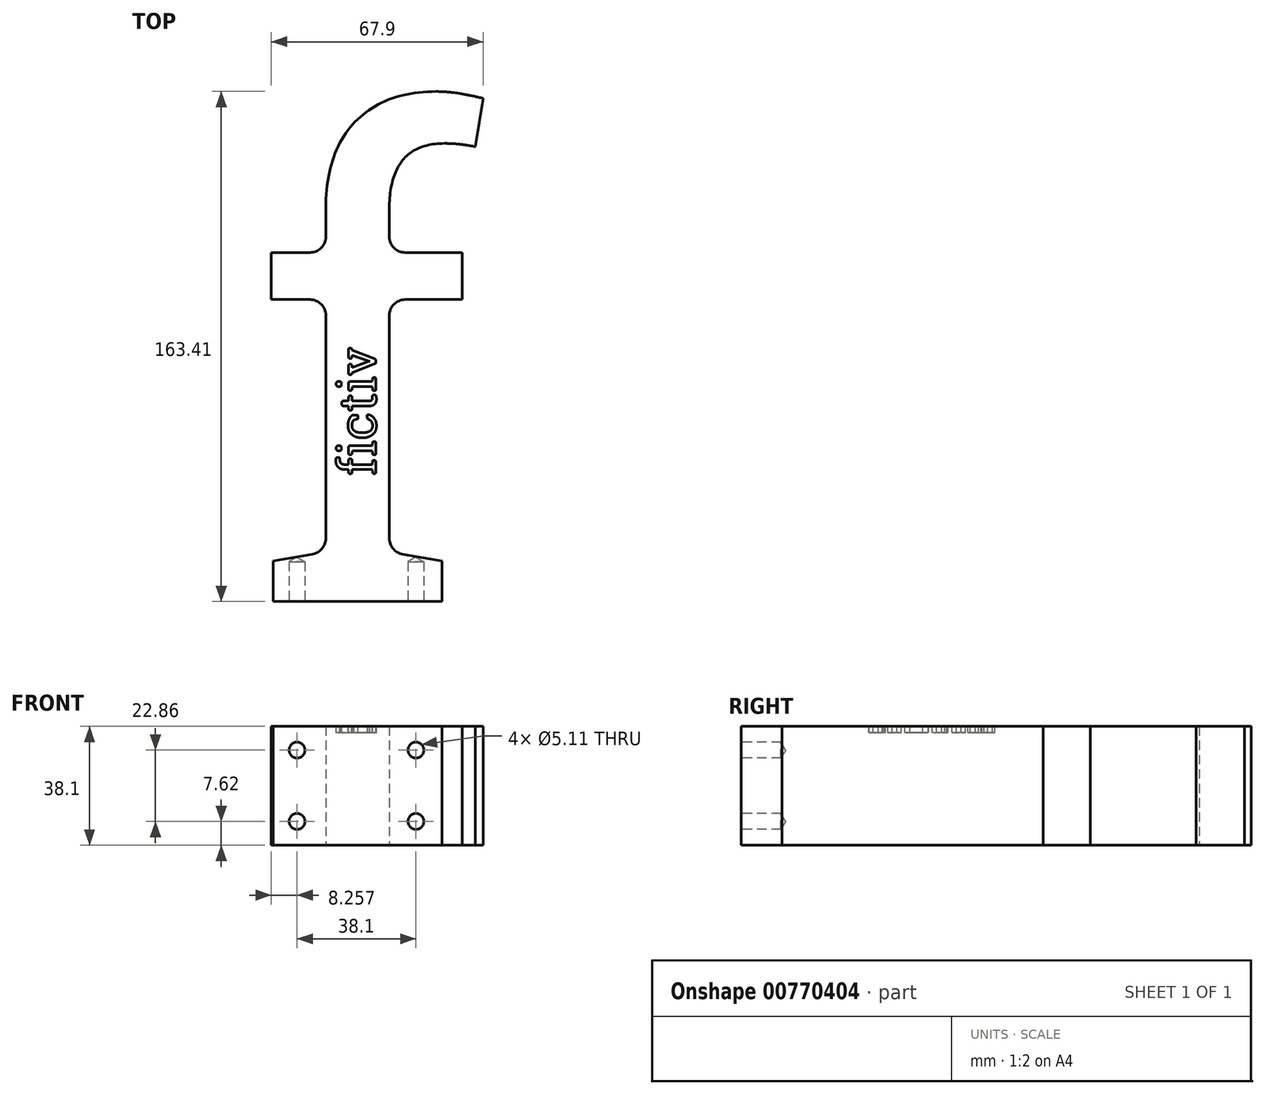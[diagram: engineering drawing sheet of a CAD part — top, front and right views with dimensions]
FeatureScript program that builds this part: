
annotation { "Feature Type Name" : "Feature", "Feature Type Description" : "" }
export const myFeature = defineFeature(function(context is Context, id is Id, definition is map)
    precondition{}
    {
        {
            var Q0;
            Q0=qCreatedBy(makeId("Top.planeOp"),FACE);
            var sketch = newSketch(context, id + "F0", { "sketchPlane" : qUnion([Q0])});
            skText(sketch, "E0", { "text": "f", "fontName": "RobotoSlab-Regular.ttf"});
            const initialGuessF0  = {"E0": [-0.0585, -0.07017, 1, 0, 0.1524]};
            skSetInitialGuess(sketch, initialGuessF0);
            skSolve(sketch);
        }
        {
            var Q0;
            Q0 = qSketchRegion(id + "F0", true);
            extrude(context, id + "F1", {"entities" : qUnion([Q0]), "depth" : 38.1 * mm, "offsetDistance" : 25 * mm});
        }
        {
            var Q0;
            Q0=makeQuery(id+"F1.opExtrude","SWEPT_EDGE",EDGE,{"disambiguationData":[OSD([sQuery(id+"F0.wireOp",EDGE,"E0.sketch_text.stroke-15"),sQuery(id+"F0.wireOp",EDGE,"E0.sketch_text.stroke-16")])]});
            var Q1;
            Q1=makeQuery(id+"F1.opExtrude","SWEPT_EDGE",EDGE,{"disambiguationData":[OSD([sQuery(id+"F0.wireOp",EDGE,"E0.sketch_text.stroke-22"),sQuery(id+"F0.wireOp",EDGE,"E0.sketch_text.stroke-23")])]});
            var Q2;
            Q2=makeQuery(id+"F1.opExtrude","SWEPT_EDGE",EDGE,{"disambiguationData":[OSD([sQuery(id+"F0.wireOp",EDGE,"E0.sketch_text.stroke-1"),sQuery(id+"F0.wireOp",EDGE,"E0.sketch_text.stroke-2")])]});
            var Q3;
            Q3=makeQuery(id+"F1.opExtrude","SWEPT_EDGE",EDGE,{"disambiguationData":[OSD([sQuery(id+"F0.wireOp",EDGE,"E0.sketch_text.stroke-12"),sQuery(id+"F0.wireOp",EDGE,"E0.sketch_text.stroke-13")])]});
            var Q4;
            Q4=makeQuery(id+"F1.opExtrude","SWEPT_EDGE",EDGE,{"disambiguationData":[OSD([sQuery(id+"F0.wireOp",EDGE,"E0.sketch_text.stroke-16"),sQuery(id+"F0.wireOp",EDGE,"E0.sketch_text.stroke-17")])]});
            var Q5;
            Q5=makeQuery(id+"F1.opExtrude","SWEPT_EDGE",EDGE,{"disambiguationData":[OSD([sQuery(id+"F0.wireOp",EDGE,"E0.sketch_text.stroke-21"),sQuery(id+"F0.wireOp",EDGE,"E0.sketch_text.stroke-22")])]});
            fillet(context, id + "F2", {"entities" : qUnion([Q0, Q1, Q2, Q3, Q4, Q5]), "radius" : 5.08 * mm, "tangentPropagation" : true, "allowEdgeOverflow" : false});
        }
        {
            var Q0;
            Q0=makeQuery(id+"F1.opExtrude","SWEPT_FACE",FACE,{"disambiguationData":[OSD([sQuery(id+"F0.wireOp",EDGE,"E0.sketch_text.stroke-19")])]});
            var sketch = newSketch(context, id + "F3", { "sketchPlane" : qUnion([Q0])});
            skPoint(sketch, "E1", {"position": v(-43, 7.62) * mm});
            skPoint(sketch, "E2", {"position": v(-43, 30.48) * mm});
            skPoint(sketch, "E3", {"position": v(-4.9, 30.48) * mm});
            skPoint(sketch, "E4", {"position": v(-4.9, 7.62) * mm});
            skSolve(sketch);
        }
        {
            var Q0;
            Q0=sQuery(id+"F3.wireOp",VERTEX,"E2");
            var Q1;
            Q1=sQuery(id+"F3.wireOp",VERTEX,"E1");
            var Q2;
            Q2=sQuery(id+"F3.wireOp",VERTEX,"E4");
            var Q3;
            Q3=sQuery(id+"F3.wireOp",VERTEX,"E3");
            var Q4;
            Q4=makeQuery(id+"F1.opExtrude","SWEPT_BODY",BODY,{"disambiguationData":[OSD([sQuery(id+"F0.wireOp",EDGE,"E0.sketch_text.stroke-0"),sQuery(id+"F0.wireOp",EDGE,"E0.sketch_text.stroke-1"),sQuery(id+"F0.wireOp",EDGE,"E0.sketch_text.stroke-2"),sQuery(id+"F0.wireOp",EDGE,"E0.sketch_text.stroke-3"),sQuery(id+"F0.wireOp",EDGE,"E0.sketch_text.stroke-4"),sQuery(id+"F0.wireOp",EDGE,"E0.sketch_text.stroke-5"),sQuery(id+"F0.wireOp",EDGE,"E0.sketch_text.stroke-6"),sQuery(id+"F0.wireOp",EDGE,"E0.sketch_text.stroke-7"),sQuery(id+"F0.wireOp",EDGE,"E0.sketch_text.stroke-8"),sQuery(id+"F0.wireOp",EDGE,"E0.sketch_text.stroke-9"),sQuery(id+"F0.wireOp",EDGE,"E0.sketch_text.stroke-10"),sQuery(id+"F0.wireOp",EDGE,"E0.sketch_text.stroke-11"),sQuery(id+"F0.wireOp",EDGE,"E0.sketch_text.stroke-12"),sQuery(id+"F0.wireOp",EDGE,"E0.sketch_text.stroke-13"),sQuery(id+"F0.wireOp",EDGE,"E0.sketch_text.stroke-14"),sQuery(id+"F0.wireOp",EDGE,"E0.sketch_text.stroke-15"),sQuery(id+"F0.wireOp",EDGE,"E0.sketch_text.stroke-16"),sQuery(id+"F0.wireOp",EDGE,"E0.sketch_text.stroke-17"),sQuery(id+"F0.wireOp",EDGE,"E0.sketch_text.stroke-18"),sQuery(id+"F0.wireOp",EDGE,"E0.sketch_text.stroke-19"),sQuery(id+"F0.wireOp",EDGE,"E0.sketch_text.stroke-20"),sQuery(id+"F0.wireOp",EDGE,"E0.sketch_text.stroke-21"),sQuery(id+"F0.wireOp",EDGE,"E0.sketch_text.stroke-22"),sQuery(id+"F0.wireOp",EDGE,"E0.sketch_text.stroke-23")])]});
            hole(context, id + "F4", {"style" : HoleStyle.SIMPLE, "endStyle" : HoleEndStyle.BLIND, "standardTappedOrClearance" : lookupTablePath({ "standard" : "ANSI", "engagement" : "75%", "pitch" : "20 tpi", "size" : "1/4", "type" : "Tapped" }), "standardBlindInLast" : lookupTablePath({ "standard" : "ANSI", "engagement" : "75%", "pitch" : "20 tpi", "size" : "1/4", "type" : "Tapped" }), "holeDiameter" : 5.1 * mm, "majorDiameter" : 6.35 * mm, "showTappedDepth" : true, "holeDepth" : 12.7 * mm, "isTappedThrough" : true, "tappedDepth" : 8.9 * mm, "tapClearance" : 3, "locations" : qUnion([Q0, Q1, Q2, Q3]), "scope" : qUnion([Q4])});
        }
        {
            var Q0;
            Q0=makeQuery(id+"F1.opExtrude","CAP_FACE",FACE,{"disambiguationData":[OSD([sQuery(id+"F0.wireOp",EDGE,"E0.sketch_text.stroke-0"),sQuery(id+"F0.wireOp",EDGE,"E0.sketch_text.stroke-1"),sQuery(id+"F0.wireOp",EDGE,"E0.sketch_text.stroke-2"),sQuery(id+"F0.wireOp",EDGE,"E0.sketch_text.stroke-3"),sQuery(id+"F0.wireOp",EDGE,"E0.sketch_text.stroke-4"),sQuery(id+"F0.wireOp",EDGE,"E0.sketch_text.stroke-5"),sQuery(id+"F0.wireOp",EDGE,"E0.sketch_text.stroke-6"),sQuery(id+"F0.wireOp",EDGE,"E0.sketch_text.stroke-7"),sQuery(id+"F0.wireOp",EDGE,"E0.sketch_text.stroke-8"),sQuery(id+"F0.wireOp",EDGE,"E0.sketch_text.stroke-9"),sQuery(id+"F0.wireOp",EDGE,"E0.sketch_text.stroke-10"),sQuery(id+"F0.wireOp",EDGE,"E0.sketch_text.stroke-11"),sQuery(id+"F0.wireOp",EDGE,"E0.sketch_text.stroke-12"),sQuery(id+"F0.wireOp",EDGE,"E0.sketch_text.stroke-13"),sQuery(id+"F0.wireOp",EDGE,"E0.sketch_text.stroke-14"),sQuery(id+"F0.wireOp",EDGE,"E0.sketch_text.stroke-15"),sQuery(id+"F0.wireOp",EDGE,"E0.sketch_text.stroke-16"),sQuery(id+"F0.wireOp",EDGE,"E0.sketch_text.stroke-17"),sQuery(id+"F0.wireOp",EDGE,"E0.sketch_text.stroke-18"),sQuery(id+"F0.wireOp",EDGE,"E0.sketch_text.stroke-19"),sQuery(id+"F0.wireOp",EDGE,"E0.sketch_text.stroke-20"),sQuery(id+"F0.wireOp",EDGE,"E0.sketch_text.stroke-21"),sQuery(id+"F0.wireOp",EDGE,"E0.sketch_text.stroke-22"),sQuery(id+"F0.wireOp",EDGE,"E0.sketch_text.stroke-23")])],"isStart":false});
            var sketch = newSketch(context, id + "F5", { "sketchPlane" : qUnion([Q0])});
            skText(sketch, "E5", { "text": "fictiv", "fontName": "RobotoSlab-Regular.ttf"});
            const initialGuessF5  = {"E5": [-0.01771, -0.02984, 0, 1, 0.012]};
            skSetInitialGuess(sketch, initialGuessF5);
            skSolve(sketch);
        }
        {
            var Q0;
            Q0 = qSketchRegion(id + "F5", true);
            var Q1;
            Q1 = qConstructionFilter(qBodyType(qCreatedBy(id + "F5" ,EDGE), BodyType.WIRE), ConstructionObject.NO);
            extrude(context, id + "F6", {"entities" : qUnion([Q0]), "operationType" : NewBodyOperationType.REMOVE, "surfaceEntities" : qUnion([Q1]), "depth" : -2 * mm, "offsetDistance" : 25 * mm});
        }
        {
            var Q0;
            Q0=makeQuery(id+"F6.boolean.opBoolean","COPY",EDGE,{"derivedFrom":makeQuery(id+"F6.opExtrude","SWEPT_EDGE",EDGE,{"disambiguationData":[OSD([sQuery(id+"F5.wireOp",EDGE,"E5.sketch_text.stroke-0"),sQuery(id+"F5.wireOp",EDGE,"E5.sketch_text.stroke-1")])]})});
            var Q1;
            Q1=makeQuery(id+"F6.boolean.opBoolean","COPY",EDGE,{"derivedFrom":makeQuery(id+"F6.opExtrude","SWEPT_EDGE",EDGE,{"disambiguationData":[OSD([sQuery(id+"F5.wireOp",EDGE,"E5.sketch_text.stroke-20"),sQuery(id+"F5.wireOp",EDGE,"E5.sketch_text.stroke-21")])]})});
            var Q2;
            Q2=makeQuery(id+"F6.boolean.opBoolean","COPY",EDGE,{"derivedFrom":makeQuery(id+"F6.opExtrude","SWEPT_EDGE",EDGE,{"disambiguationData":[OSD([sQuery(id+"F5.wireOp",EDGE,"E5.sketch_text.stroke-24"),sQuery(id+"F5.wireOp",EDGE,"E5.sketch_text.stroke-33")])]})});
            var Q3;
            Q3=makeQuery(id+"F6.boolean.opBoolean","COPY",EDGE,{"derivedFrom":makeQuery(id+"F6.opExtrude","SWEPT_EDGE",EDGE,{"disambiguationData":[OSD([sQuery(id+"F5.wireOp",EDGE,"E5.sketch_text.stroke-27"),sQuery(id+"F5.wireOp",EDGE,"E5.sketch_text.stroke-28")])]})});
            var Q4;
            Q4=makeQuery(id+"F6.boolean.opBoolean","COPY",EDGE,{"derivedFrom":makeQuery(id+"F6.opExtrude","SWEPT_EDGE",EDGE,{"disambiguationData":[OSD([sQuery(id+"F5.wireOp",EDGE,"E5.sketch_text.stroke-77"),sQuery(id+"F5.wireOp",EDGE,"E5.sketch_text.stroke-78")])]})});
            var Q5;
            Q5=makeQuery(id+"F6.boolean.opBoolean","COPY",EDGE,{"derivedFrom":makeQuery(id+"F6.opExtrude","SWEPT_EDGE",EDGE,{"disambiguationData":[OSD([sQuery(id+"F5.wireOp",EDGE,"E5.sketch_text.stroke-79"),sQuery(id+"F5.wireOp",EDGE,"E5.sketch_text.stroke-80")])]})});
            var Q6;
            Q6=makeQuery(id+"F6.boolean.opBoolean","COPY",EDGE,{"derivedFrom":makeQuery(id+"F6.opExtrude","SWEPT_EDGE",EDGE,{"disambiguationData":[OSD([sQuery(id+"F5.wireOp",EDGE,"E5.sketch_text.stroke-84"),sQuery(id+"F5.wireOp",EDGE,"E5.sketch_text.stroke-85")])]})});
            var Q7;
            Q7=makeQuery(id+"F6.boolean.opBoolean","COPY",EDGE,{"derivedFrom":makeQuery(id+"F6.opExtrude","SWEPT_EDGE",EDGE,{"disambiguationData":[OSD([sQuery(id+"F5.wireOp",EDGE,"E5.sketch_text.stroke-35"),sQuery(id+"F5.wireOp",EDGE,"E5.sketch_text.stroke-36")])]})});
            var Q8;
            Q8=makeQuery(id+"F6.boolean.opBoolean","COPY",EDGE,{"derivedFrom":makeQuery(id+"F6.opExtrude","SWEPT_EDGE",EDGE,{"disambiguationData":[OSD([sQuery(id+"F5.wireOp",EDGE,"E5.sketch_text.stroke-81"),sQuery(id+"F5.wireOp",EDGE,"E5.sketch_text.stroke-90")])]})});
            var Q9;
            Q9=makeQuery(id+"F6.boolean.opBoolean","COPY",EDGE,{"derivedFrom":makeQuery(id+"F6.opExtrude","SWEPT_EDGE",EDGE,{"disambiguationData":[OSD([sQuery(id+"F5.wireOp",EDGE,"E5.sketch_text.stroke-92"),sQuery(id+"F5.wireOp",EDGE,"E5.sketch_text.stroke-93")])]})});
            var Q10;
            Q10=makeQuery(id+"F6.boolean.opBoolean","COPY",EDGE,{"derivedFrom":makeQuery(id+"F6.opExtrude","SWEPT_EDGE",EDGE,{"disambiguationData":[OSD([sQuery(id+"F5.wireOp",EDGE,"E5.sketch_text.stroke-110"),sQuery(id+"F5.wireOp",EDGE,"E5.sketch_text.stroke-111")])]})});
            var Q11;
            Q11=makeQuery(id+"F6.boolean.opBoolean","COPY",EDGE,{"derivedFrom":makeQuery(id+"F6.opExtrude","SWEPT_EDGE",EDGE,{"disambiguationData":[OSD([sQuery(id+"F5.wireOp",EDGE,"E5.sketch_text.stroke-102"),sQuery(id+"F5.wireOp",EDGE,"E5.sketch_text.stroke-103")])]})});
            var Q12;
            Q12=makeQuery(id+"F6.boolean.opBoolean","COPY",EDGE,{"derivedFrom":makeQuery(id+"F6.opExtrude","SWEPT_EDGE",EDGE,{"disambiguationData":[OSD([sQuery(id+"F5.wireOp",EDGE,"E5.sketch_text.stroke-19"),sQuery(id+"F5.wireOp",EDGE,"E5.sketch_text.stroke-20")])]})});
            var Q13;
            Q13=makeQuery(id+"F6.boolean.opBoolean","COPY",EDGE,{"derivedFrom":makeQuery(id+"F6.opExtrude","SWEPT_EDGE",EDGE,{"disambiguationData":[OSD([sQuery(id+"F5.wireOp",EDGE,"E5.sketch_text.stroke-0"),sQuery(id+"F5.wireOp",EDGE,"E5.sketch_text.stroke-23")])]})});
            var Q14;
            Q14=makeQuery(id+"F6.boolean.opBoolean","COPY",EDGE,{"derivedFrom":makeQuery(id+"F6.opExtrude","SWEPT_EDGE",EDGE,{"disambiguationData":[OSD([sQuery(id+"F5.wireOp",EDGE,"E5.sketch_text.stroke-32"),sQuery(id+"F5.wireOp",EDGE,"E5.sketch_text.stroke-33")])]})});
            var Q15;
            Q15=makeQuery(id+"F6.boolean.opBoolean","COPY",EDGE,{"derivedFrom":makeQuery(id+"F6.opExtrude","SWEPT_EDGE",EDGE,{"disambiguationData":[OSD([sQuery(id+"F5.wireOp",EDGE,"E5.sketch_text.stroke-26"),sQuery(id+"F5.wireOp",EDGE,"E5.sketch_text.stroke-27")])]})});
            var Q16;
            Q16=makeQuery(id+"F6.boolean.opBoolean","COPY",EDGE,{"derivedFrom":makeQuery(id+"F6.opExtrude","SWEPT_EDGE",EDGE,{"disambiguationData":[OSD([sQuery(id+"F5.wireOp",EDGE,"E5.sketch_text.stroke-34"),sQuery(id+"F5.wireOp",EDGE,"E5.sketch_text.stroke-35")])]})});
            var Q17;
            Q17=makeQuery(id+"F6.boolean.opBoolean","COPY",EDGE,{"derivedFrom":makeQuery(id+"F6.opExtrude","SWEPT_EDGE",EDGE,{"disambiguationData":[OSD([sQuery(id+"F5.wireOp",EDGE,"E5.sketch_text.stroke-76"),sQuery(id+"F5.wireOp",EDGE,"E5.sketch_text.stroke-77")])]})});
            var Q18;
            Q18=makeQuery(id+"F6.boolean.opBoolean","COPY",EDGE,{"derivedFrom":makeQuery(id+"F6.opExtrude","SWEPT_EDGE",EDGE,{"disambiguationData":[OSD([sQuery(id+"F5.wireOp",EDGE,"E5.sketch_text.stroke-91"),sQuery(id+"F5.wireOp",EDGE,"E5.sketch_text.stroke-92")])]})});
            var Q19;
            Q19=makeQuery(id+"F6.boolean.opBoolean","COPY",EDGE,{"derivedFrom":makeQuery(id+"F6.opExtrude","SWEPT_EDGE",EDGE,{"disambiguationData":[OSD([sQuery(id+"F5.wireOp",EDGE,"E5.sketch_text.stroke-83"),sQuery(id+"F5.wireOp",EDGE,"E5.sketch_text.stroke-84")])]})});
            var Q20;
            Q20=makeQuery(id+"F6.boolean.opBoolean","COPY",EDGE,{"derivedFrom":makeQuery(id+"F6.opExtrude","SWEPT_EDGE",EDGE,{"disambiguationData":[OSD([sQuery(id+"F5.wireOp",EDGE,"E5.sketch_text.stroke-89"),sQuery(id+"F5.wireOp",EDGE,"E5.sketch_text.stroke-90")])]})});
            var Q21;
            Q21=makeQuery(id+"F6.boolean.opBoolean","COPY",EDGE,{"derivedFrom":makeQuery(id+"F6.opExtrude","SWEPT_EDGE",EDGE,{"disambiguationData":[OSD([sQuery(id+"F5.wireOp",EDGE,"E5.sketch_text.stroke-109"),sQuery(id+"F5.wireOp",EDGE,"E5.sketch_text.stroke-110")])]})});
            var Q22;
            Q22=makeQuery(id+"F6.boolean.opBoolean","COPY",EDGE,{"derivedFrom":makeQuery(id+"F6.opExtrude","SWEPT_EDGE",EDGE,{"disambiguationData":[OSD([sQuery(id+"F5.wireOp",EDGE,"E5.sketch_text.stroke-107"),sQuery(id+"F5.wireOp",EDGE,"E5.sketch_text.stroke-108")])]})});
            var Q23;
            Q23=makeQuery(id+"F6.boolean.opBoolean","COPY",EDGE,{"derivedFrom":makeQuery(id+"F6.opExtrude","SWEPT_EDGE",EDGE,{"disambiguationData":[OSD([sQuery(id+"F5.wireOp",EDGE,"E5.sketch_text.stroke-52"),sQuery(id+"F5.wireOp",EDGE,"E5.sketch_text.stroke-53")])]})});
            var Q24;
            Q24=makeQuery(id+"F6.boolean.opBoolean","COPY",EDGE,{"derivedFrom":makeQuery(id+"F6.opExtrude","SWEPT_EDGE",EDGE,{"disambiguationData":[OSD([sQuery(id+"F5.wireOp",EDGE,"E5.sketch_text.stroke-18"),sQuery(id+"F5.wireOp",EDGE,"E5.sketch_text.stroke-19")])]})});
            var Q25;
            Q25=makeQuery(id+"F6.boolean.opBoolean","COPY",EDGE,{"derivedFrom":makeQuery(id+"F6.opExtrude","SWEPT_EDGE",EDGE,{"disambiguationData":[OSD([sQuery(id+"F5.wireOp",EDGE,"E5.sketch_text.stroke-31"),sQuery(id+"F5.wireOp",EDGE,"E5.sketch_text.stroke-32")])]})});
            var Q26;
            Q26=makeQuery(id+"F6.boolean.opBoolean","COPY",EDGE,{"derivedFrom":makeQuery(id+"F6.opExtrude","SWEPT_EDGE",EDGE,{"disambiguationData":[OSD([sQuery(id+"F5.wireOp",EDGE,"E5.sketch_text.stroke-51"),sQuery(id+"F5.wireOp",EDGE,"E5.sketch_text.stroke-52")])]})});
            var Q27;
            Q27=makeQuery(id+"F6.boolean.opBoolean","COPY",EDGE,{"derivedFrom":makeQuery(id+"F6.opExtrude","SWEPT_EDGE",EDGE,{"disambiguationData":[OSD([sQuery(id+"F5.wireOp",EDGE,"E5.sketch_text.stroke-70"),sQuery(id+"F5.wireOp",EDGE,"E5.sketch_text.stroke-71")])]})});
            var Q28;
            Q28=makeQuery(id+"F6.boolean.opBoolean","COPY",EDGE,{"derivedFrom":makeQuery(id+"F6.opExtrude","SWEPT_EDGE",EDGE,{"disambiguationData":[OSD([sQuery(id+"F5.wireOp",EDGE,"E5.sketch_text.stroke-88"),sQuery(id+"F5.wireOp",EDGE,"E5.sketch_text.stroke-89")])]})});
            var Q29;
            Q29=makeQuery(id+"F6.boolean.opBoolean","COPY",EDGE,{"derivedFrom":makeQuery(id+"F6.opExtrude","SWEPT_EDGE",EDGE,{"disambiguationData":[OSD([sQuery(id+"F5.wireOp",EDGE,"E5.sketch_text.stroke-106"),sQuery(id+"F5.wireOp",EDGE,"E5.sketch_text.stroke-107")])]})});
            var Q30;
            Q30=makeQuery(id+"F6.boolean.opBoolean","COPY",EDGE,{"derivedFrom":makeQuery(id+"F6.opExtrude","SWEPT_EDGE",EDGE,{"disambiguationData":[OSD([sQuery(id+"F5.wireOp",EDGE,"E5.sketch_text.stroke-104"),sQuery(id+"F5.wireOp",EDGE,"E5.sketch_text.stroke-105")])]})});
            var Q31;
            Q31=makeQuery(id+"F6.boolean.opBoolean","COPY",EDGE,{"derivedFrom":makeQuery(id+"F6.opExtrude","SWEPT_EDGE",EDGE,{"disambiguationData":[OSD([sQuery(id+"F5.wireOp",EDGE,"E5.sketch_text.stroke-95"),sQuery(id+"F5.wireOp",EDGE,"E5.sketch_text.stroke-112")])]})});
            var Q32;
            Q32=makeQuery(id+"F6.boolean.opBoolean","COPY",EDGE,{"derivedFrom":makeQuery(id+"F6.opExtrude","SWEPT_EDGE",EDGE,{"disambiguationData":[OSD([sQuery(id+"F5.wireOp",EDGE,"E5.sketch_text.stroke-91"),sQuery(id+"F5.wireOp",EDGE,"E5.sketch_text.stroke-94")])]})});
            var Q33;
            Q33=makeQuery(id+"F6.boolean.opBoolean","COPY",EDGE,{"derivedFrom":makeQuery(id+"F6.opExtrude","SWEPT_EDGE",EDGE,{"disambiguationData":[OSD([sQuery(id+"F5.wireOp",EDGE,"E5.sketch_text.stroke-63"),sQuery(id+"F5.wireOp",EDGE,"E5.sketch_text.stroke-64")])]})});
            var Q34;
            Q34=makeQuery(id+"F6.boolean.opBoolean","COPY",EDGE,{"derivedFrom":makeQuery(id+"F6.opExtrude","SWEPT_EDGE",EDGE,{"disambiguationData":[OSD([sQuery(id+"F5.wireOp",EDGE,"E5.sketch_text.stroke-34"),sQuery(id+"F5.wireOp",EDGE,"E5.sketch_text.stroke-37")])]})});
            var Q35;
            Q35=makeQuery(id+"F6.boolean.opBoolean","COPY",EDGE,{"derivedFrom":makeQuery(id+"F6.opExtrude","SWEPT_EDGE",EDGE,{"disambiguationData":[OSD([sQuery(id+"F5.wireOp",EDGE,"E5.sketch_text.stroke-14"),sQuery(id+"F5.wireOp",EDGE,"E5.sketch_text.stroke-15")])]})});
            var Q36;
            Q36=makeQuery(id+"F6.boolean.opBoolean","COPY",EDGE,{"derivedFrom":makeQuery(id+"F6.opExtrude","SWEPT_EDGE",EDGE,{"disambiguationData":[OSD([sQuery(id+"F5.wireOp",EDGE,"E5.sketch_text.stroke-7"),sQuery(id+"F5.wireOp",EDGE,"E5.sketch_text.stroke-8")])]})});
            var Q37;
            Q37=makeQuery(id+"F6.boolean.opBoolean","COPY",EDGE,{"derivedFrom":makeQuery(id+"F6.opExtrude","SWEPT_EDGE",EDGE,{"disambiguationData":[OSD([sQuery(id+"F5.wireOp",EDGE,"E5.sketch_text.stroke-103"),sQuery(id+"F5.wireOp",EDGE,"E5.sketch_text.stroke-104")])]})});
            var Q38;
            Q38=makeQuery(id+"F6.boolean.opBoolean","COPY",EDGE,{"derivedFrom":makeQuery(id+"F6.opExtrude","SWEPT_EDGE",EDGE,{"disambiguationData":[OSD([sQuery(id+"F5.wireOp",EDGE,"E5.sketch_text.stroke-111"),sQuery(id+"F5.wireOp",EDGE,"E5.sketch_text.stroke-112")])]})});
            var Q39;
            Q39=makeQuery(id+"F6.boolean.opBoolean","COPY",EDGE,{"derivedFrom":makeQuery(id+"F6.opExtrude","SWEPT_EDGE",EDGE,{"disambiguationData":[OSD([sQuery(id+"F5.wireOp",EDGE,"E5.sketch_text.stroke-93"),sQuery(id+"F5.wireOp",EDGE,"E5.sketch_text.stroke-94")])]})});
            var Q40;
            Q40=makeQuery(id+"F6.boolean.opBoolean","COPY",EDGE,{"derivedFrom":makeQuery(id+"F6.opExtrude","SWEPT_EDGE",EDGE,{"disambiguationData":[OSD([sQuery(id+"F5.wireOp",EDGE,"E5.sketch_text.stroke-61"),sQuery(id+"F5.wireOp",EDGE,"E5.sketch_text.stroke-80")])]})});
            var Q41;
            Q41=makeQuery(id+"F6.boolean.opBoolean","COPY",EDGE,{"derivedFrom":makeQuery(id+"F6.opExtrude","SWEPT_EDGE",EDGE,{"disambiguationData":[OSD([sQuery(id+"F5.wireOp",EDGE,"E5.sketch_text.stroke-62"),sQuery(id+"F5.wireOp",EDGE,"E5.sketch_text.stroke-63")])]})});
            var Q42;
            Q42=makeQuery(id+"F6.boolean.opBoolean","COPY",EDGE,{"derivedFrom":makeQuery(id+"F6.opExtrude","SWEPT_EDGE",EDGE,{"disambiguationData":[OSD([sQuery(id+"F5.wireOp",EDGE,"E5.sketch_text.stroke-85"),sQuery(id+"F5.wireOp",EDGE,"E5.sketch_text.stroke-86")])]})});
            var Q43;
            Q43=makeQuery(id+"F6.boolean.opBoolean","COPY",EDGE,{"derivedFrom":makeQuery(id+"F6.opExtrude","SWEPT_EDGE",EDGE,{"disambiguationData":[OSD([sQuery(id+"F5.wireOp",EDGE,"E5.sketch_text.stroke-87"),sQuery(id+"F5.wireOp",EDGE,"E5.sketch_text.stroke-88")])]})});
            var Q44;
            Q44=makeQuery(id+"F6.boolean.opBoolean","COPY",EDGE,{"derivedFrom":makeQuery(id+"F6.opExtrude","SWEPT_EDGE",EDGE,{"disambiguationData":[OSD([sQuery(id+"F5.wireOp",EDGE,"E5.sketch_text.stroke-50"),sQuery(id+"F5.wireOp",EDGE,"E5.sketch_text.stroke-51")])]})});
            var Q45;
            Q45=makeQuery(id+"F6.boolean.opBoolean","COPY",EDGE,{"derivedFrom":makeQuery(id+"F6.opExtrude","SWEPT_EDGE",EDGE,{"disambiguationData":[OSD([sQuery(id+"F5.wireOp",EDGE,"E5.sketch_text.stroke-40"),sQuery(id+"F5.wireOp",EDGE,"E5.sketch_text.stroke-41")])]})});
            var Q46;
            Q46=makeQuery(id+"F6.boolean.opBoolean","COPY",EDGE,{"derivedFrom":makeQuery(id+"F6.opExtrude","SWEPT_EDGE",EDGE,{"disambiguationData":[OSD([sQuery(id+"F5.wireOp",EDGE,"E5.sketch_text.stroke-36"),sQuery(id+"F5.wireOp",EDGE,"E5.sketch_text.stroke-37")])]})});
            var Q47;
            Q47=makeQuery(id+"F6.boolean.opBoolean","COPY",EDGE,{"derivedFrom":makeQuery(id+"F6.opExtrude","SWEPT_EDGE",EDGE,{"disambiguationData":[OSD([sQuery(id+"F5.wireOp",EDGE,"E5.sketch_text.stroke-6"),sQuery(id+"F5.wireOp",EDGE,"E5.sketch_text.stroke-7")])]})});
            var Q48;
            Q48=makeQuery(id+"F6.boolean.opBoolean","COPY",EDGE,{"derivedFrom":makeQuery(id+"F6.opExtrude","SWEPT_EDGE",EDGE,{"disambiguationData":[OSD([sQuery(id+"F5.wireOp",EDGE,"E5.sketch_text.stroke-28"),sQuery(id+"F5.wireOp",EDGE,"E5.sketch_text.stroke-29")])]})});
            var Q49;
            Q49=makeQuery(id+"F6.boolean.opBoolean","COPY",EDGE,{"derivedFrom":makeQuery(id+"F6.opExtrude","SWEPT_EDGE",EDGE,{"disambiguationData":[OSD([sQuery(id+"F5.wireOp",EDGE,"E5.sketch_text.stroke-13"),sQuery(id+"F5.wireOp",EDGE,"E5.sketch_text.stroke-14")])]})});
            var Q50;
            Q50=makeQuery(id+"F6.boolean.opBoolean","COPY",EDGE,{"derivedFrom":makeQuery(id+"F6.opExtrude","SWEPT_EDGE",EDGE,{"disambiguationData":[OSD([sQuery(id+"F5.wireOp",EDGE,"E5.sketch_text.stroke-69"),sQuery(id+"F5.wireOp",EDGE,"E5.sketch_text.stroke-70")])]})});
            var Q51;
            Q51=makeQuery(id+"F6.boolean.opBoolean","COPY",EDGE,{"derivedFrom":makeQuery(id+"F6.opExtrude","SWEPT_EDGE",EDGE,{"disambiguationData":[OSD([sQuery(id+"F5.wireOp",EDGE,"E5.sketch_text.stroke-39"),sQuery(id+"F5.wireOp",EDGE,"E5.sketch_text.stroke-40")])]})});
            fillet(context, id + "F7", {"entities" : qUnion([Q0, Q1, Q2, Q3, Q4, Q5, Q6, Q7, Q8, Q9, Q10, Q11, Q12, Q13, Q14, Q15, Q16, Q17, Q18, Q19, Q20, Q21, Q22, Q23, Q24, Q25, Q26, Q27, Q28, Q29, Q30, Q31, Q32, Q33, Q34, Q35, Q36, Q37, Q38, Q39, Q40, Q41, Q42, Q43, Q44, Q45, Q46, Q47, Q48, Q49, Q50, Q51]), "radius" : .5 * mm, "tangentPropagation" : true, "allowEdgeOverflow" : false});
        }
    });
